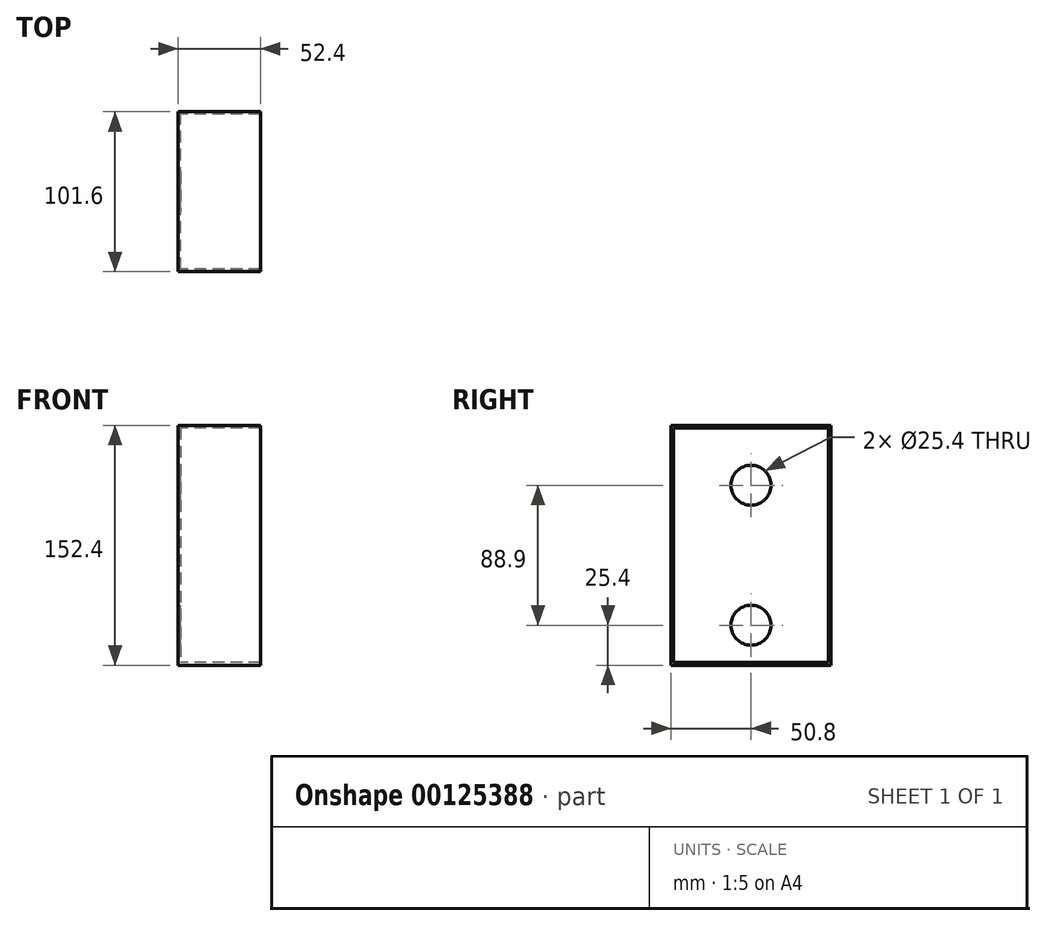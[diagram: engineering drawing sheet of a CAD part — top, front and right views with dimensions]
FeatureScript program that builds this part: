
annotation { "Feature Type Name" : "Feature", "Feature Type Description" : "" }
export const myFeature = defineFeature(function(context is Context, id is Id, definition is map)
    precondition{}
    {
        {
            var Q0;
            Q0=qCreatedBy(makeId("Right.planeOp"),FACE);
            var sketch = newSketch(context, id + "F0", { "sketchPlane" : qUnion([Q0])});
            skLineSegment(sketch, "E0", {"start": v(0, 76.2) * mm, "end": v(50.8, 76.2) * mm});
            skLineSegment(sketch, "E1", {"start": v(50.8, 76.2) * mm, "end": v(50.8, 0) * mm});
            skLineSegment(sketch, "E2.MirrorCS", {"start": v(0, 76.2) * mm, "end": v(-50.8, 76.2) * mm});
            skLineSegment(sketch, "E3.MirrorCS", {"start": v(-50.8, 76.2) * mm, "end": v(-50.8, 0) * mm});
            skLineSegment(sketch, "E4.MirrorCS", {"start": v(-50.8, -76.2) * mm, "end": v(-50.8, 0) * mm});
            skLineSegment(sketch, "E5.MirrorCS", {"start": v(0, -76.2) * mm, "end": v(-50.8, -76.2) * mm});
            skLineSegment(sketch, "E6.MirrorCS", {"start": v(0, -76.2) * mm, "end": v(50.8, -76.2) * mm});
            skLineSegment(sketch, "E7.MirrorCS", {"start": v(50.8, -76.2) * mm, "end": v(50.8, 0) * mm});
            skLineSegment(sketch, "E8.bottom", {"start": v(-49.2, 74.61) * mm, "end": v(49.2, 74.61) * mm});
            skLineSegment(sketch, "E8.top", {"start": v(-49.2, -74.6) * mm, "end": v(49.2, -74.6) * mm});
            skLineSegment(sketch, "E8.left", {"start": v(-49.2, 74.61) * mm, "end": v(-49.2, -74.6) * mm});
            skLineSegment(sketch, "E8.right", {"start": v(49.2, 74.61) * mm, "end": v(49.2, -74.6) * mm});
            skSolve(sketch);
        }
        {
            var Q0;
            Q0 = qSketchRegion(id + "F0", true);
            var Q1;
            Q1=makeQuery(id+"F0.imprint","IMPRINT",FACE,{"disambiguationData":[TD([[makeQuery(id+"F0.imprint","IMPRINT",EDGE,{"derivedFrom":sQuery(id+"F0.wireOp",EDGE,"E8.bottom")}),-1.0]])]});
            extrude(context, id + "F1", {"entities" : qUnion([Q0, Q1]), "oppositeDirection" : true, "depth" : 1.6 * mm});
        }
        {
            var Q0;
            Q0=makeQuery(id+"F0.imprint","IMPRINT",FACE,{"disambiguationData":[TD([[makeQuery(id+"F0.imprint","IMPRINT",EDGE,{"derivedFrom":sQuery(id+"F0.wireOp",EDGE,"E0")}),-1.0]])]});
            extrude(context, id + "F2", {"entities" : qUnion([Q0]), "operationType" : NewBodyOperationType.ADD, "depth" : 50.8 * mm});
        }
        {
            var Q0;
            Q0=makeQuery(id+"F1.opExtrude","CAP_FACE",FACE,{"disambiguationData":[OSD([sQuery(id+"F0.wireOp",EDGE,"E0"),sQuery(id+"F0.wireOp",EDGE,"E1"),sQuery(id+"F0.wireOp",EDGE,"E2.MirrorCS"),sQuery(id+"F0.wireOp",EDGE,"E3.MirrorCS"),sQuery(id+"F0.wireOp",EDGE,"E4.MirrorCS"),sQuery(id+"F0.wireOp",EDGE,"E5.MirrorCS"),sQuery(id+"F0.wireOp",EDGE,"E6.MirrorCS"),sQuery(id+"F0.wireOp",EDGE,"E7.MirrorCS")])],"isStart":true});
            var sketch = newSketch(context, id + "F3", { "sketchPlane" : qUnion([Q0])});
            skCircle(sketch, "E9", {"center": v(0, 38.1) * mm, "radius": 12.7 * mm});
            skCircle(sketch, "E10", {"center": v(0, -50.8) * mm, "radius": 12.7 * mm});
            skSolve(sketch);
        }
        {
            var Q0;
            Q0 = qSketchRegion(id + "F3", true);
            extrude(context, id + "F4", {"entities" : qUnion([Q0]), "operationType" : NewBodyOperationType.REMOVE, "oppositeDirection" : true, "depth" : 1.6 * mm});
        }
    });
